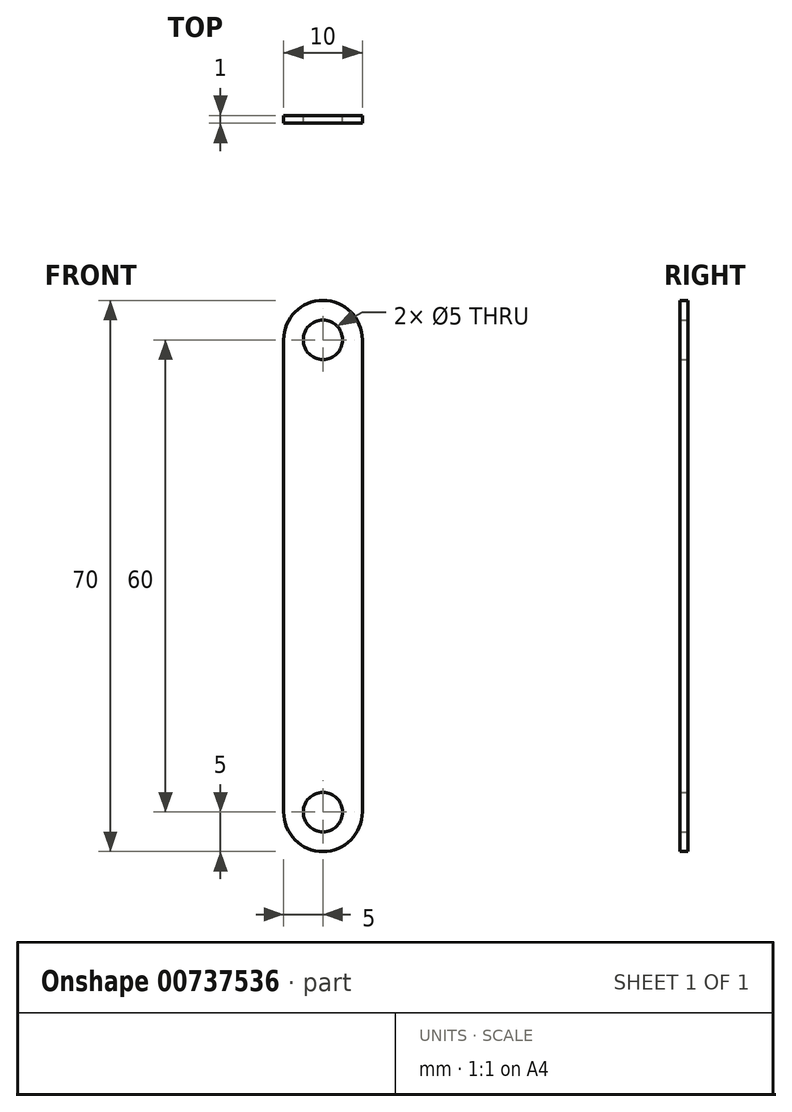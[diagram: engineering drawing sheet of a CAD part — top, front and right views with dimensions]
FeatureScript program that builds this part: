
annotation { "Feature Type Name" : "Feature", "Feature Type Description" : "" }
export const myFeature = defineFeature(function(context is Context, id is Id, definition is map)
    precondition{}
    {
        {
            var Q0;
            Q0=qCreatedBy(makeId("Front.planeOp"),FACE);
            var sketch = newSketch(context, id + "F0", { "sketchPlane" : qUnion([Q0])});
            skArc(sketch, "E0", {"start": v(5, 30) * mm, "mid": v(0, 35) * mm, "end": v(-5, 30) * mm});
            skArc(sketch, "E1", {"start": v(-5, -30) * mm, "mid": v(0, -35) * mm, "end": v(5, -30) * mm});
            skLineSegment(sketch, "E2", {"start": v(-5, 30) * mm, "end": v(-5, -30) * mm});
            skLineSegment(sketch, "E3", {"start": v(5, 30) * mm, "end": v(5, -30) * mm});
            skCircle(sketch, "E4", {"center": v(0, 30) * mm, "radius": 2.5 * mm});
            skCircle(sketch, "E5", {"center": v(0, -30) * mm, "radius": 2.5 * mm});
            skSolve(sketch);
        }
        {
            var Q0;
            Q0 = qSketchRegion(id + "F0", true);
            extrude(context, id + "F1", {"entities" : qUnion([Q0]), "depth" : 1 * mm, "offsetDistance" : 25 * mm});
        }
    });
